# Revit family: EWS2
name_source: partatom
category: Generic Models
revit_build: Autodesk Revit LT 2017 (Build: 20160225_1515(x64)
units: mm (PartAtom-declared; Revit-internal decimal feet)

## family parameters
Always vertical = No
Can host rebar = No
Cut with Voids When Loaded = No
Part Type = Normal
Room Calculation Point = No
Round Connector Dimension = Use Diameter
Shared = No
Work Plane-Based = Yes

## types (1)
- NBS Standard Parameters
    BIMObjectName = Metpro_metprolibrary_standardsocketoutlets_switchandsocketboxes_metal
    Default Elevation = 1219 mm
    Description = EWS2 -25mm 1 Gang Switch & Socket Box
    DurationUnit = year
    Finish = Pre Galvanised
    Keynote = Compliant to BS4662 & LU Standard 1-085 (For Use on Surface & Sub-Surface Locations)
    ManufacturerName = Metpro Ltd
    ManufacturerURL = www.metpro.co.uk
    Material = Sheet Steel To Comply with BS4667
    ModelReference = EWS2
    NBSDescription = Standard Socket Outlets
    NBSReference = 90-60-25/345
    NominalHeight = 26 mm
    NominalLength = 75 mm
    NominalWidth = 75 mm
    ProductInformation = www.metpro.co.uk/pdf/ews2.pdf
    Shape = Square
    Size = 25mm
    Uniclass2 = Pr_65_72_97_84
    Version = 1
    WarrantyDurationUnit = 1 year
    Weight = 0.09Kg

## geometry (parser evidence)
native form markers: Sweep x2
no freeform markers — native parametric forms only
